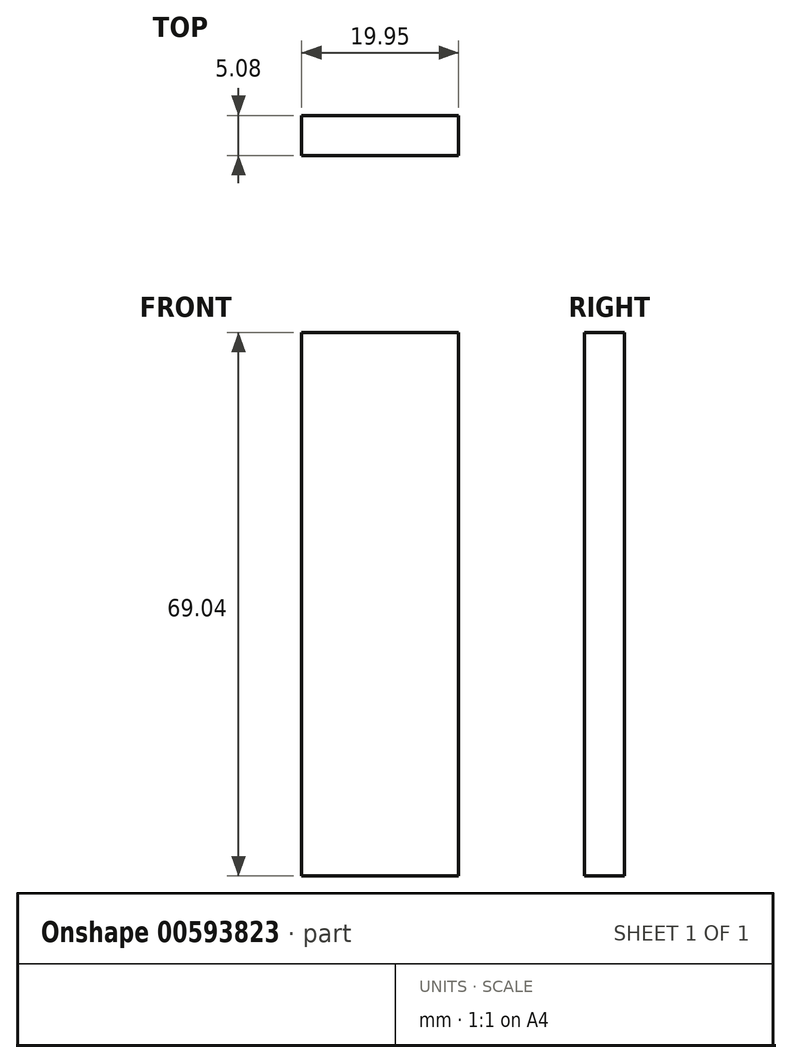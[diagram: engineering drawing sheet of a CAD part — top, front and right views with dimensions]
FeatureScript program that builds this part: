
annotation { "Feature Type Name" : "Feature", "Feature Type Description" : "" }
export const myFeature = defineFeature(function(context is Context, id is Id, definition is map)
    precondition{}
    {
        {
            var Q0;
            Q0=qCreatedBy(makeId("Front.planeOp"),FACE);
            var sketch = newSketch(context, id + "F0", { "sketchPlane" : qUnion([Q0])});
            skLineSegment(sketch, "E0", {"start": v(-19.8, 44.05) * mm, "end": v(-19.8, -25) * mm});
            skLineSegment(sketch, "E1", {"start": v(-19.8, -25) * mm, "end": v(0.15, -25) * mm});
            skLineSegment(sketch, "E2", {"start": v(0.15, -25) * mm, "end": v(0.15, 44.05) * mm});
            skLineSegment(sketch, "E3", {"start": v(0.15, 44.05) * mm, "end": v(-19.8, 44.05) * mm});
            skSolve(sketch);
        }
        {
            var Q0;
            Q0=makeQuery(id+"F0.imprint","IMPRINT",FACE,{"disambiguationData":[TD([[makeQuery(id+"F0.imprint","IMPRINT",EDGE,{"derivedFrom":sQuery(id+"F0.wireOp",EDGE,"E0")}),1.0]])]});
            extrude(context, id + "F1", {"entities" : qUnion([Q0]), "endBound" : BoundingType.SYMMETRIC, "depth" : 5.08 * mm, "offsetDistance" : 25.4 * mm});
        }
    });
